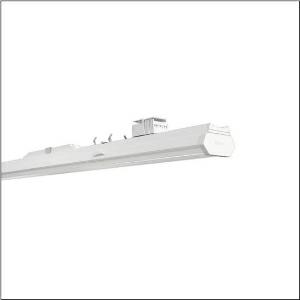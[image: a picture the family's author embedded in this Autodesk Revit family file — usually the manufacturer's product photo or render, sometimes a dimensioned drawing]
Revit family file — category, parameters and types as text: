
# Revit family: licross_r__11_protected_mo_51td127n485g_dbd9
name_source: partatom
category: Lighting Fixtures
units: mm (PartAtom-declared; Revit-internal decimal feet)

## family parameters
Cut with Voids When Loaded = No
Host = Face
Light Source = No
Part Type = Normal
Room Calculation Point = No
Round Connector Dimension = Use Diameter
Shared = No

## types (1)
- Licross® 11 Protected MO (1 x LED, 8720 lm, 48.6 W, 4000K)
    Apparent Load = 49 VA
    CIE Flux Codes = 73 92 98 99 100
    Color Rendering = 80
    Color Temperature = 4000K
    Default Elevation = 1800 mm
    Description = Licross® 11 Protected MO, luminaire insert, of sheet steel, galvanised, coil coated, white, length: 1.500mm, width: 90mm, height: 101mm, LED rated luminous flux: 8.720lm, light colour: 840, control gear: ON/OFF, with plug, 3-pole, with phase selection, mains connection: 220..240V, AC, 50/60Hz, rated input power: 49W, halogen-free wiring, primary light control with lens, of plastic, primary optical cover: cover, of PMMA, light emission: direct distribution, primary light characteristic: symmetric, protection rating (complete): IP54, insulation class (complete): insulation class I (protective earthing), certification: CE, ENEC, VDE, UKCA, protection symbol: D if used in an environment with non-conductive dust loads with corresponding accessories, impact resistance: IK06, permissible ambient temperature for indoor applications: -25..+35°C, corresponds to IFS (International Featured Standards) requirements for safety and quality in the food industry, reducing of maximum allowable ambient temperature of 5°C with ceiling mounting, LABS conformity tested according to VDMA 24364:2018-05, packaging unit: 1 piece
    Height = 92 mm
    Lamp = 1 x LED
    Lamp Light Flux = 8720 lm
    Lamp Power = 48.6 W
    Lamp count = 1
    Length = 1500 mm
    Luminous efficacy = 179 lm/W
    Manufacturer = Siteco
    ModVariant = No
    Model = 51TD127N485G
    Mounting Place = Ceiling
    Mounting Type = Pendant
    Number of Poles = 1
    OnlyDefault = Yes
    Power Factor = 1
    Product Name = Licross® 11 Protected MO
    Product group = luminaire insert
    ProductGroupID = 902
    Protection Class = Protection class I
    Protection Degree = IP 54
    RLX_Detail_Level = 1
    RLX_Emergency_Light_Flux = 0 lm
    RLX_Emergency_Type = 0
    RLX_Emergency_Type_DB = No
    RlxData = <blob elided: 20665 chars, md5=caba3c42>
    Socket = socket
    Standby Power = 0 W
    System Light Flux = 8720 lm
    System Power = 49 W
    Type Comments = Product without accessories
    Type Image = l_1256145.jpg
    URL = http://relux.com
    VarID = ---
    Voltage = 0 V
    Weight = 0.00 kg
    Width = 88 mm

## geometry (parser evidence)
native form markers: Blend x4, Sweep x12
no freeform markers — native parametric forms only
